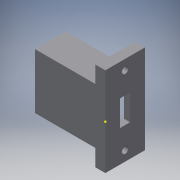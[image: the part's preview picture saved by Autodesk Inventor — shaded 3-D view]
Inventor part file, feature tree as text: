
AUTODESK INVENTOR PART (.ipt)
format: ipt  version: 2018 (Build 220112000, 112)  size: 176,128 bytes
history: native  units: mm
features: extrude x5, sketch x3
ambient origin geometry x8: Origin, YZ Plane, XZ Plane, XY Plane, X Axis, Y Axis, Z Axis, Center Point
bodies: Solid1 (feature_tree)
feature tree (8):
  extrude  "Extrusion1"  Depth=13.0mm
  extrude  "Extrusion2"  Depth=45.0mm
  sketch  "Sketch3"  dims[d0=5.0mm d1=13.0mm]
  extrude  "Extrusion5"  Depth=20.0mm
  extrude  "Extrusion8"  Depth=11.0mm
  extrude  "Extrusion10"  Depth=27.0mm TaperAngle=0.0deg
  sketch  "Sketch6"  dims[d2=20.0mm d3=45.0mm]
  sketch  "Sketch8"  dims[d4=5.0mm d5=0.0mm d6=20.0mm d7=11.0mm d9=27.0mm d10=0.0mm d11=13.0mm d12=11.0mm d17=5.0mm d18=3.2mm d19=3.2mm d20=5.0mm d21=3.2mm d22=3.2mm d23=5.0mm d24=5.0mm d25=5.0mm d26=0.0mm d27=4.5mm d32=14.0mm d33=14.0mm d34=3.5mm d35=0.0mm d36=12.0mm d39=2.0mm d40=0.0mm d41=10.0mm]
